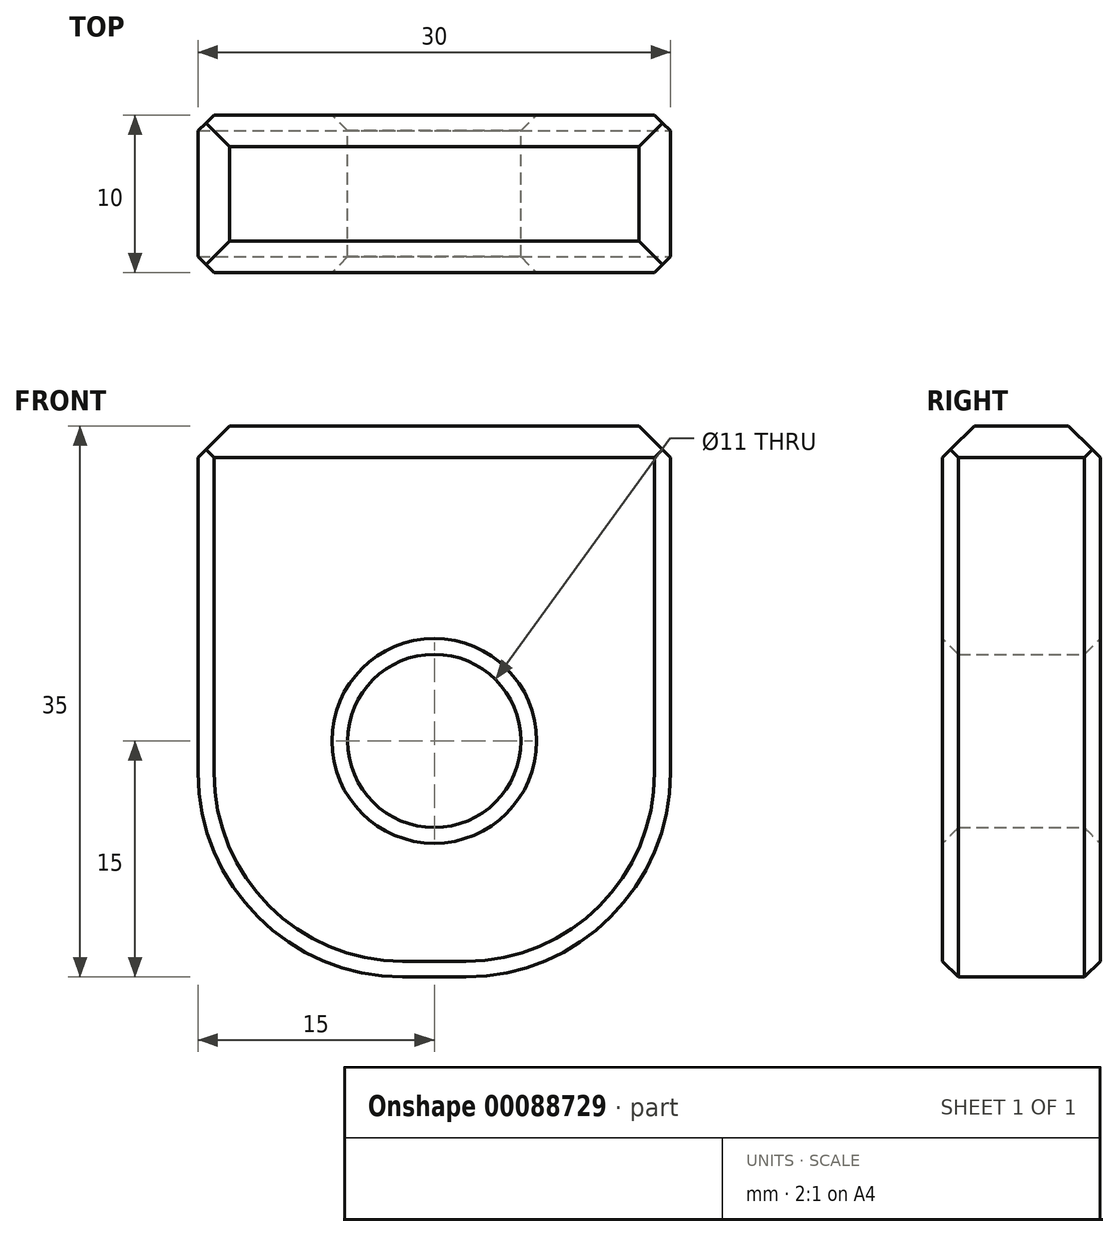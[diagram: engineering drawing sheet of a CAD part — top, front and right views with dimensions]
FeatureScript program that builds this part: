
annotation { "Feature Type Name" : "Feature", "Feature Type Description" : "" }
export const myFeature = defineFeature(function(context is Context, id is Id, definition is map)
    precondition{}
    {
        {
            var Q0;
            Q0=qCreatedBy(makeId("Front.planeOp"),FACE);
            var sketch = newSketch(context, id + "F0", { "sketchPlane" : qUnion([Q0])});
            skLineSegment(sketch, "E0.bottom", {"start": v(-15, 17.5) * mm, "end": v(15, 17.5) * mm});
            skLineSegment(sketch, "E0.top", {"start": v(-15, -17.5) * mm, "end": v(15, -17.5) * mm});
            skLineSegment(sketch, "E0.left", {"start": v(-15, 17.5) * mm, "end": v(-15, -17.5) * mm});
            skLineSegment(sketch, "E0.right", {"start": v(15, 17.5) * mm, "end": v(15, -17.5) * mm});
            skPoint(sketch, "E0.middle", {"position": v(0, 0) * mm});
            skPoint(sketch, "E1.endSnap0", {"position": v(0, -17.5) * mm});
            skCircle(sketch, "E2", {"center": v(0, -2.5) * mm, "radius": 5.5 * mm});
            skSolve(sketch);
        }
        {
            var Q0;
            Q0 = qSketchRegion(id + "F0", true);
            var Q1;
            Q1=makeQuery(id+"F0.imprint","IMPRINT",FACE,{"disambiguationData":[TD([[makeQuery(id+"F0.imprint","IMPRINT",EDGE,{"derivedFrom":sQuery(id+"F0.wireOp",EDGE,"E0.bottom")}),-1.0]])]});
            extrude(context, id + "F1", {"entities" : qUnion([Q0, Q1]), "depth" : 10 * mm});
        }
        {
            var Q0;
            Q0=makeQuery(id+"F1.opExtrude","SWEPT_EDGE",EDGE,{"disambiguationData":[OSD([sQuery(id+"F0.wireOp",EDGE,"E0.top"),sQuery(id+"F0.wireOp",EDGE,"E0.right")])]});
            var Q1;
            Q1=makeQuery(id+"F1.opExtrude","SWEPT_EDGE",EDGE,{"disambiguationData":[OSD([sQuery(id+"F0.wireOp",EDGE,"E0.top"),sQuery(id+"F0.wireOp",EDGE,"E0.left")])]});
            fillet(context, id + "F2", {"entities" : qUnion([Q0, Q1]), "radius" : 13 * mm, "tangentPropagation" : true, "allowEdgeOverflow" : false});
        }
        {
            var Q0;
            Q0=makeQuery(id+"F1.opExtrude","SWEPT_FACE",FACE,{"disambiguationData":[OSD([sQuery(id+"F0.wireOp",EDGE,"E0.bottom")])]});
            chamfer(context, id + "F3", {"entities" : qUnion([Q0]), "width" : 2 * mm, "tangentPropagation" : true});
        }
        {
            var Q0;
            Q0=makeQuery(id+"F1.opExtrude","CAP_EDGE",EDGE,{"disambiguationData":[OSD([sQuery(id+"F0.wireOp",EDGE,"E0.left")])],"isStart":false});
            var Q1;
            Q1=makeQuery(id+"F1.opExtrude","CAP_EDGE",EDGE,{"disambiguationData":[OSD([sQuery(id+"F0.wireOp",EDGE,"E0.left")])],"isStart":true});
            chamfer(context, id + "F4", {"entities" : qUnion([Q0, Q1]), "width" : 1 * mm, "tangentPropagation" : true});
        }
        {
            var Q0;
            Q0=makeQuery(id+"F1.opExtrude","SWEPT_FACE",FACE,{"disambiguationData":[OSD([sQuery(id+"F0.wireOp",EDGE,"E2")])]});
            chamfer(context, id + "F5", {"entities" : qUnion([Q0]), "width" : 1 * mm, "tangentPropagation" : true});
        }
    });
